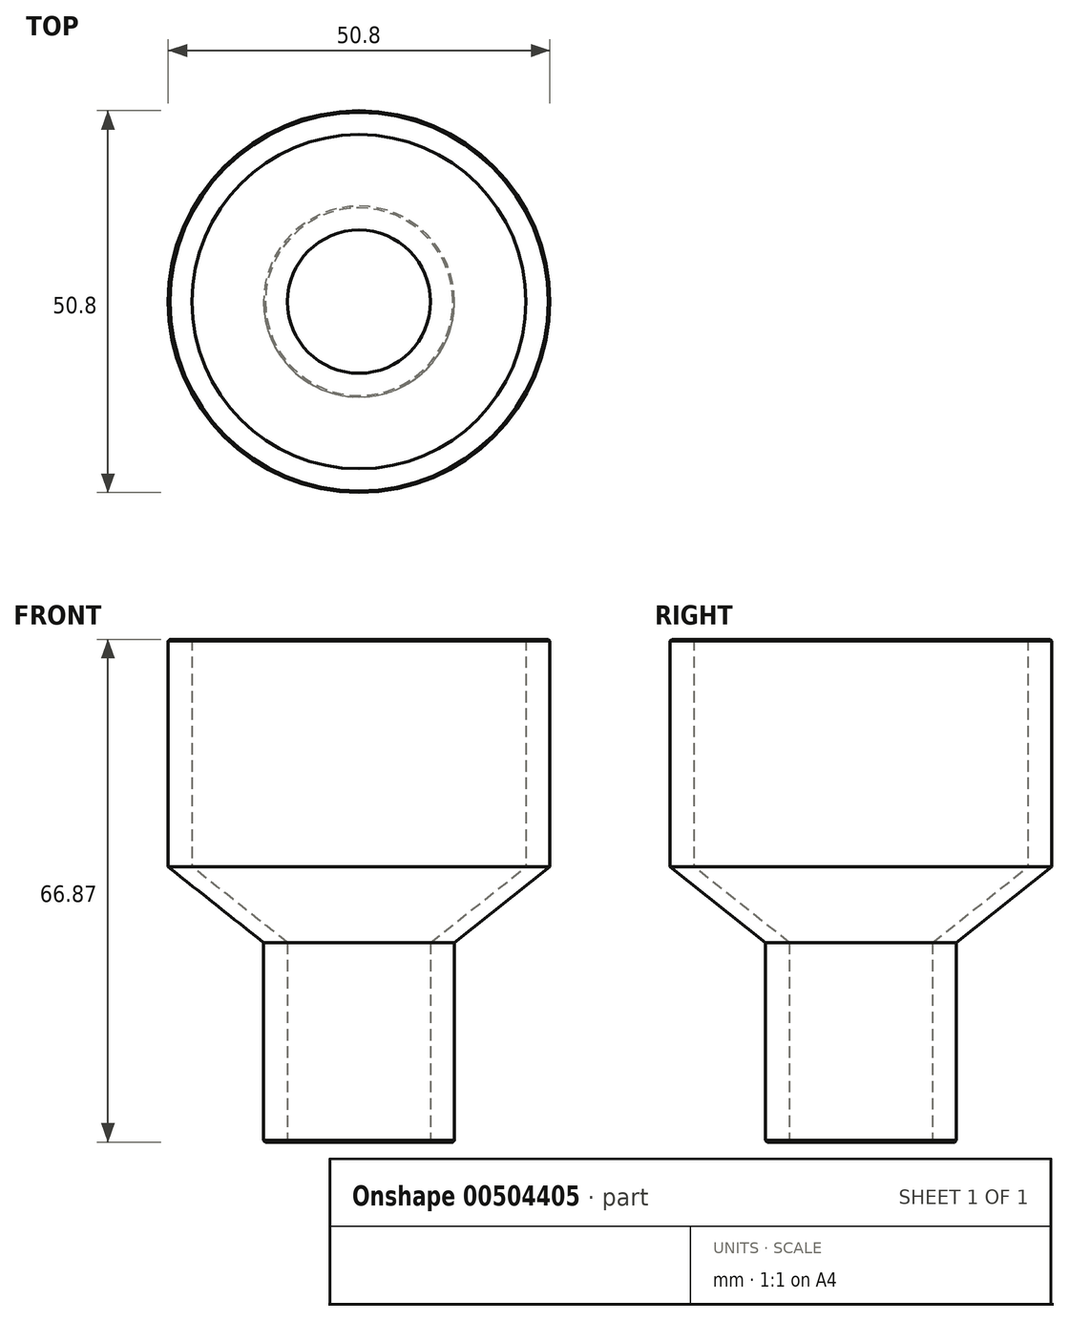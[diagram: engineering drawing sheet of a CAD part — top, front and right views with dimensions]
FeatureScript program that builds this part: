
annotation { "Feature Type Name" : "Feature", "Feature Type Description" : "" }
export const myFeature = defineFeature(function(context is Context, id is Id, definition is map)
    precondition{}
    {
        {
            var Q0;
            Q0=qCreatedBy(makeId("Right.planeOp"),FACE);
            var sketch = newSketch(context, id + "F0", { "sketchPlane" : qUnion([Q0])});
            skLineSegment(sketch, "E0.bottom", {"start": v(22.23, 30.26) * mm, "end": v(25.4, 30.26) * mm});
            skLineSegment(sketch, "E0.top", {"start": v(22.23, 0) * mm, "end": v(25.4, 0) * mm});
            skLineSegment(sketch, "E0.left", {"start": v(22.23, 30.26) * mm, "end": v(22.23, 0) * mm});
            skLineSegment(sketch, "E0.right", {"start": v(25.4, 30.26) * mm, "end": v(25.4, 0) * mm});
            skLineSegment(sketch, "E1.bottom", {"start": v(12.7, -10.09) * mm, "end": v(9.53, -10.09) * mm});
            skLineSegment(sketch, "E1.top", {"start": v(12.7, -36.6) * mm, "end": v(9.53, -36.6) * mm});
            skLineSegment(sketch, "E1.left", {"start": v(12.7, -10.09) * mm, "end": v(12.7, -36.6) * mm});
            skLineSegment(sketch, "E1.right", {"start": v(9.53, -10.09) * mm, "end": v(9.53, -36.6) * mm});
            skLineSegment(sketch, "E2", {"start": v(25.4, 0) * mm, "end": v(12.7, -10.09) * mm});
            skLineSegment(sketch, "E3", {"start": v(22.23, 0) * mm, "end": v(9.52, -10.09) * mm});
            skLineSegment(sketch, "E4", {"start": v(9.53, -36.6) * mm, "end": v(0, -36.6) * mm});
            skLineSegment(sketch, "E5", {"start": v(0, -36.6) * mm, "end": v(0, -15.69) * mm});
            skSolve(sketch);
        }
        {
            var Q0;
            Q0=makeQuery(id+"F0.imprint","IMPRINT",FACE,{"disambiguationData":[TD([[makeQuery(id+"F0.imprint","IMPRINT",EDGE,{"derivedFrom":sQuery(id+"F0.wireOp",EDGE,"E0.bottom")}),-1.0]])]});
            var Q1;
            Q1=makeQuery(id+"F0.imprint","IMPRINT",FACE,{"disambiguationData":[TD([[makeQuery(id+"F0.imprint","IMPRINT",EDGE,{"derivedFrom":sQuery(id+"F0.wireOp",EDGE,"E0.top")}),-1.0]])]});
            var Q2;
            Q2=makeQuery(id+"F0.imprint","IMPRINT",FACE,{"disambiguationData":[TD([[makeQuery(id+"F0.imprint","IMPRINT",EDGE,{"derivedFrom":sQuery(id+"F0.wireOp",EDGE,"E1.bottom")}),1.0]])]});
            var Q3;
            Q3=sQuery(id+"F0.wireOp",EDGE,"E5");
            revolve(context, id + "F1", {"entities" : qUnion([Q0, Q1, Q2]), "axis" : qUnion([Q3]), "revolveType" : RevolveType.FULL});
        }
        {
            var Q0;
            Q0=makeQuery(id+"F1.opRevolve","SWEPT_EDGE",EDGE,{"disambiguationData":[OSD([sQuery(id+"F0.wireOp",EDGE,"E1.top"),sQuery(id+"F0.wireOp",EDGE,"E1.left")])]});
            var Q1;
            Q1=makeQuery(id+"F1.opRevolve","SWEPT_EDGE",EDGE,{"disambiguationData":[OSD([sQuery(id+"F0.wireOp",EDGE,"E0.bottom"),sQuery(id+"F0.wireOp",EDGE,"E0.right")])]});
            chamfer(context, id + "F2", {"entities" : qUnion([Q0, Q1]), "width" : 0.23 * mm, "tangentPropagation" : true});
        }
    });
